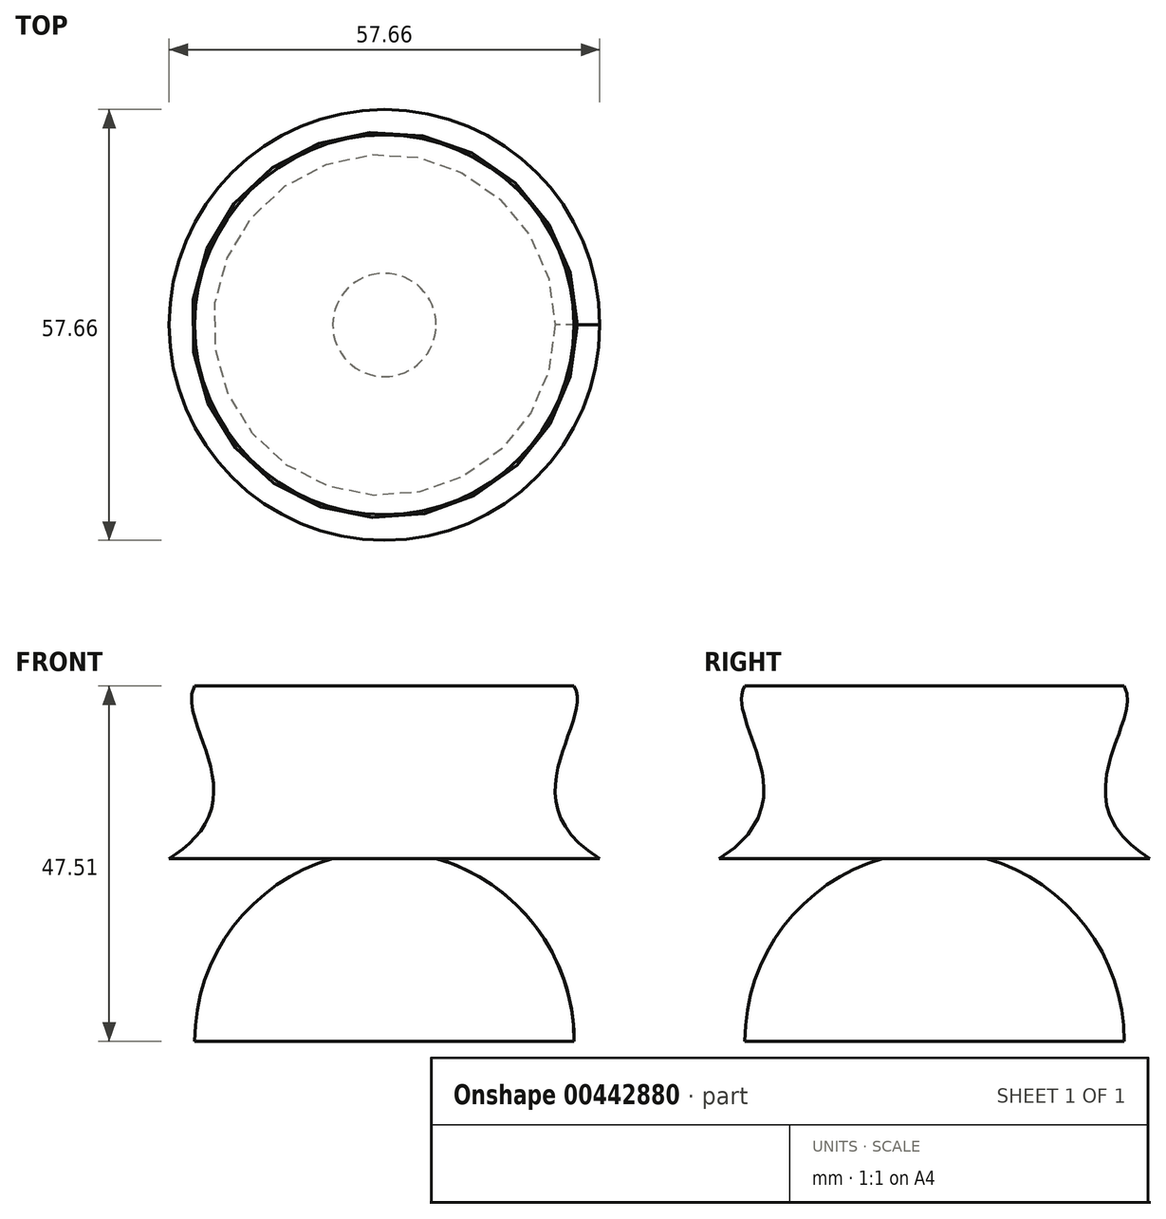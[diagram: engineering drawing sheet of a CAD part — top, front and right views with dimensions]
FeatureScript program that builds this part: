
annotation { "Feature Type Name" : "Feature", "Feature Type Description" : "" }
export const myFeature = defineFeature(function(context is Context, id is Id, definition is map)
    precondition{}
    {
        {
            var Q0;
            Q0=qCreatedBy(makeId("Front.planeOp"),FACE);
            var sketch = newSketch(context, id + "F0", { "sketchPlane" : qUnion([Q0])});
            skArc(sketch, "E0", {"start": v(-6.92, 24.44) * mm, "mid": v(-20.26, 15.32) * mm, "end": v(-25.4, 0) * mm});
            skLineSegment(sketch, "E1", {"start": v(-6.92, 24.44) * mm, "end": v(-28.83, 24.44) * mm});
            skLineSegment(sketch, "E2", {"start": v(-25.4, 47.5) * mm, "end": v(0, 47.5) * mm});
            skLineSegment(sketch, "E3", {"start": v(-25.4, 0) * mm, "end": v(0, 0) * mm});
            skLineSegment(sketch, "E4", {"start": v(0, 47.5) * mm, "end": v(0, 0) * mm});
            skFitSpline(sketch, "E5", {"points": [v(-25.4, 47.5) * mm, v(-28.83, 24.44) * mm], "startDerivative": vector(-8.42, -14.03) * mm, "endDerivative": vector(-38.34, -23.38) * mm});
            skSolve(sketch);
        }
        {
            var Q0;
            Q0=makeQuery(id+"F0.imprint","IMPRINT",FACE,{"disambiguationData":[TD([[makeQuery(id+"F0.imprint","IMPRINT",EDGE,{"derivedFrom":sQuery(id+"F0.wireOp",EDGE,"E0")}),1.0]])]});
            var Q1;
            Q1=sQuery(id+"F0.wireOp",EDGE,"E4");
            revolve(context, id + "F1", {"entities" : qUnion([Q0]), "axis" : qUnion([Q1]), "revolveType" : RevolveType.FULL});
        }
    });
